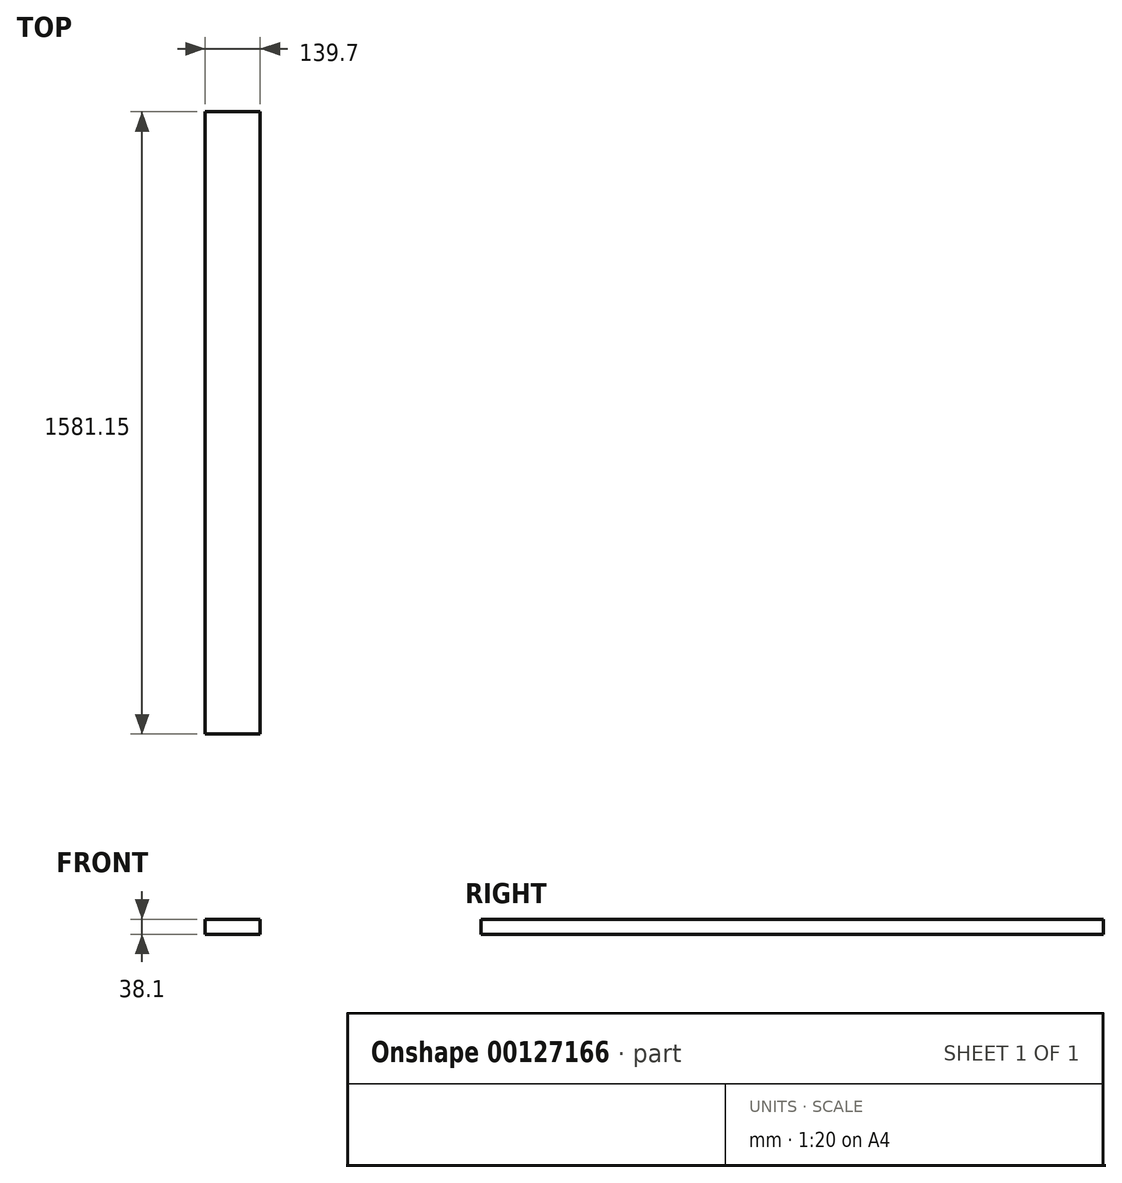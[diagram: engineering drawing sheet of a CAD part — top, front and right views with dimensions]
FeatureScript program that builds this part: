
annotation { "Feature Type Name" : "Feature", "Feature Type Description" : "" }
export const myFeature = defineFeature(function(context is Context, id is Id, definition is map)
    precondition{}
    {
        {
            var Q0;
            Q0=qCreatedBy(makeId("Front.planeOp"),FACE);
            var sketch = newSketch(context, id + "F0", { "sketchPlane" : qUnion([Q0])});
            skLineSegment(sketch, "E0.bottom", {"start": v(69.85, -19.05) * mm, "end": v(-69.85, -19.05) * mm});
            skLineSegment(sketch, "E0.top", {"start": v(69.85, 19.05) * mm, "end": v(-69.85, 19.05) * mm});
            skLineSegment(sketch, "E0.left", {"start": v(69.85, -19.05) * mm, "end": v(69.85, 19.05) * mm});
            skLineSegment(sketch, "E0.right", {"start": v(-69.85, -19.05) * mm, "end": v(-69.85, 19.05) * mm});
            skPoint(sketch, "E0.middle", {"position": v(0, 0) * mm});
            skSolve(sketch);
        }
        {
            var Q0;
            Q0=qSketchRegion(id+"F0",true);
            extrude(context, id + "F1", {"entities" : qUnion([Q0]), "depth" : 1581.15 * mm, "offsetDistance" : 25.4 * mm});
        }
    });
